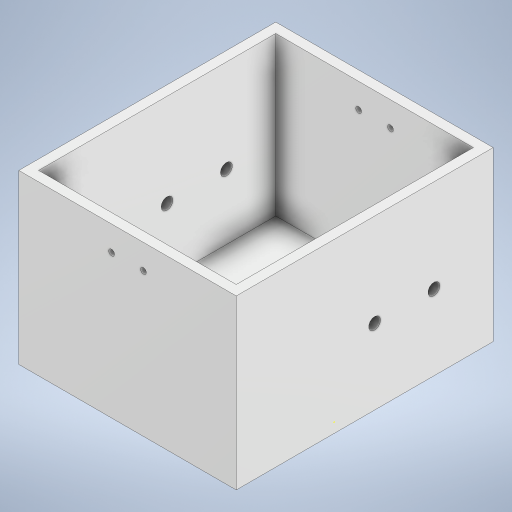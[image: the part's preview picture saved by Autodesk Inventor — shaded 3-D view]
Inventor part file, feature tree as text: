
AUTODESK INVENTOR PART (.ipt)
format: ipt  version: 2023 (Build 270158000, 158)  size: 204,800 bytes
history: native  units: in
note: dims shown in document units (in); Inventor stores cm internally (conversion verified against a paired STEP export)
features: sketch x5, hole x2, other x1, extrude x1, delete_face x1, thicken_offset x1
ambient origin geometry x8: Origin, YZ Plane, XZ Plane, XY Plane, X Axis, Y Axis, Z Axis, Center Point
bodies: Body1 (feature_tree)
feature tree (11):
  other  "hollow"
  sketch  "Sketch1"  dims[d0=3.937in d1=4.7244in]
  extrude  "Extrusion1"  Depth=4.7244in
  delete_face  "Delete Face1"
  thicken_offset  "Thicken1"
  sketch  "Sketch3"  dims[d5=0.2362in d6=0.2362in d7=0.1575in d8=0.0787in d9=90.0deg d10=0.315in d11=0.8108in]
  hole  "Hole1"  [1 undecoded]
  hole  "Hole2"  [1 undecoded]
  sketch  "Sketch2"  dims[d2=3.1496in d3=0.0in d4=0.1969in]
  sketch  "Sketch4"  dims[d12=0.1181in d13=0.2362in d14=0.1575in d15=0.0787in d16=90.0deg d17=0.315in d18=0.8108in]
  sketch  "Sketch5"
note: 2 required parameter values undecoded (feature->parameter linkage not recoverable at this tier; creation-order binding heuristic only, values carry confidence <= 0.55)
